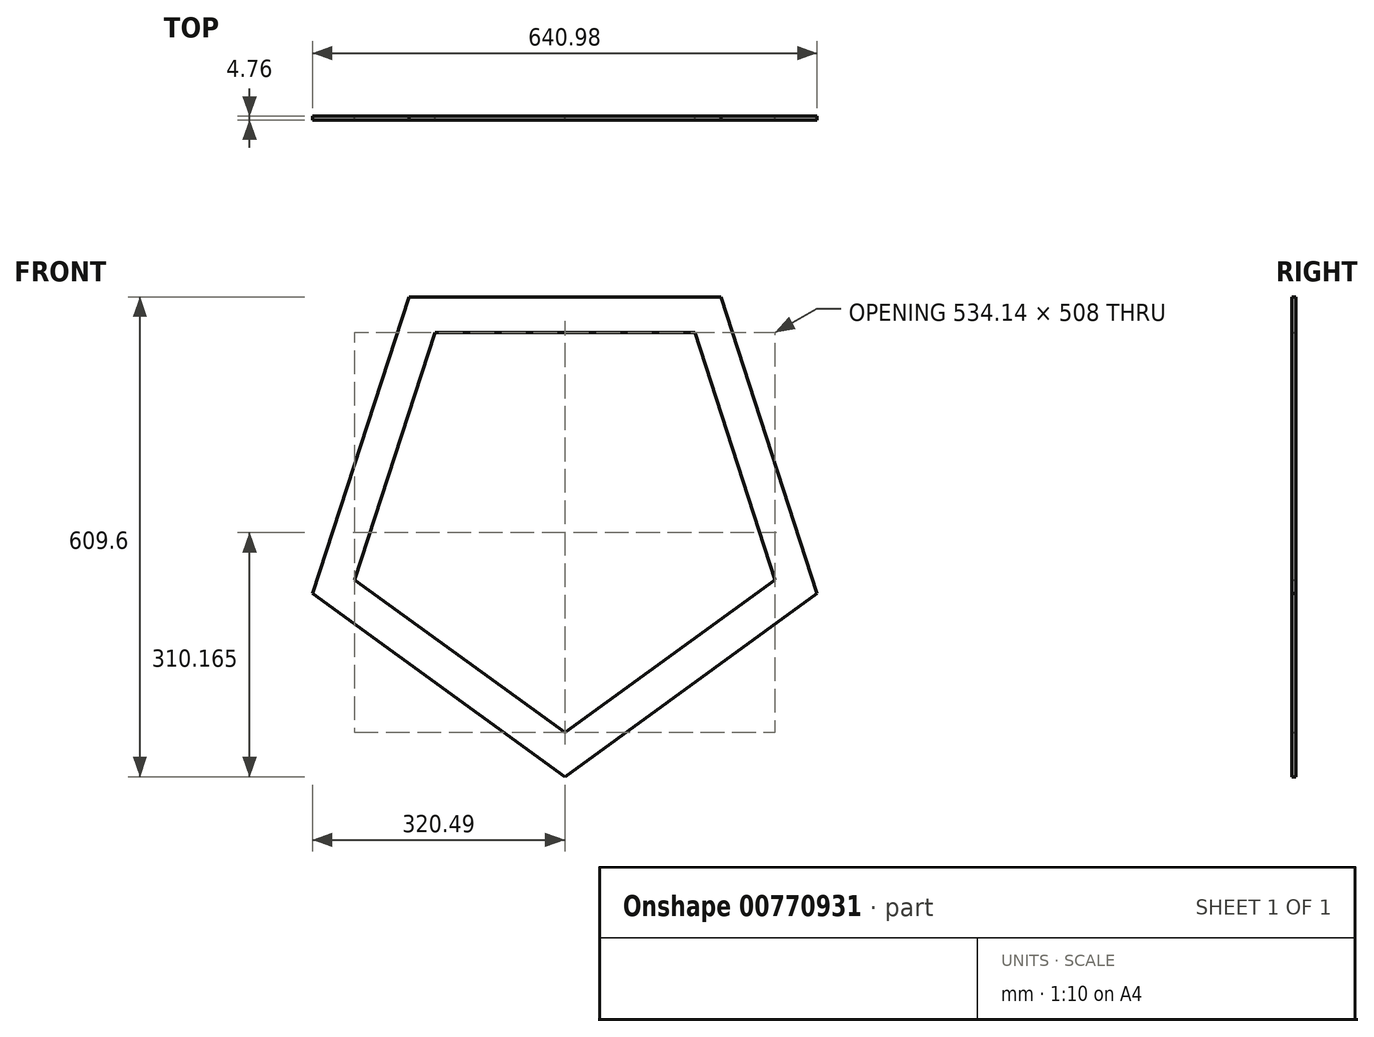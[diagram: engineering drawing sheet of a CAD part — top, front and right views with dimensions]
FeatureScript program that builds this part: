
annotation { "Feature Type Name" : "Feature", "Feature Type Description" : "" }
export const myFeature = defineFeature(function(context is Context, id is Id, definition is map)
    precondition{}
    {
        {
            var Q0;
            Q0=qCreatedBy(makeId("Front.planeOp"),FACE);
            var sketch = newSketch(context, id + "F0", { "sketchPlane" : qUnion([Q0])});
            skCircle(sketch, "E0.cCircle", {"center": v(0, 0) * mm, "radius": 272.62 * mm, "construction": true});
            skLineSegment(sketch, "E0.0", {"start": v(-198.07, 272.62) * mm, "end": v(198.07, 272.62) * mm});
            skLineSegment(sketch, "E0.1", {"start": v(198.07, 272.62) * mm, "end": v(320.49, -104.13) * mm});
            skLineSegment(sketch, "E0.2", {"start": v(320.49, -104.13) * mm, "end": v(0, -336.98) * mm});
            skLineSegment(sketch, "E0.3", {"start": v(0, -336.98) * mm, "end": v(-320.49, -104.13) * mm});
            skLineSegment(sketch, "E0.4", {"start": v(-320.49, -104.13) * mm, "end": v(-198.07, 272.62) * mm});
            skPoint(sketch, "E0.0.midPoint", {"position": v(0, 272.62) * mm});
            skCircle(sketch, "E1.cCircle", {"center": v(0, 0) * mm, "radius": 227.18 * mm, "construction": true});
            skLineSegment(sketch, "E1.0", {"start": v(-165.06, 227.18) * mm, "end": v(165.06, 227.18) * mm});
            skLineSegment(sketch, "E1.1", {"start": v(165.06, 227.18) * mm, "end": v(267.07, -86.78) * mm});
            skLineSegment(sketch, "E1.2", {"start": v(267.07, -86.78) * mm, "end": v(0, -280.82) * mm});
            skLineSegment(sketch, "E1.3", {"start": v(0, -280.82) * mm, "end": v(-267.07, -86.78) * mm});
            skLineSegment(sketch, "E1.4", {"start": v(-267.07, -86.78) * mm, "end": v(-165.06, 227.18) * mm});
            skPoint(sketch, "E1.0.midPoint", {"position": v(0, 227.18) * mm});
            skSolve(sketch);
        }
        {
            var Q0;
            Q0=qSketchRegion(id+"F0",true);
            extrude(context, id + "F1", {"entities" : qUnion([Q0]), "endBound" : BoundingType.SYMMETRIC, "depth" : 4.76 * mm, "offsetDistance" : 25.4 * mm});
        }
    });
